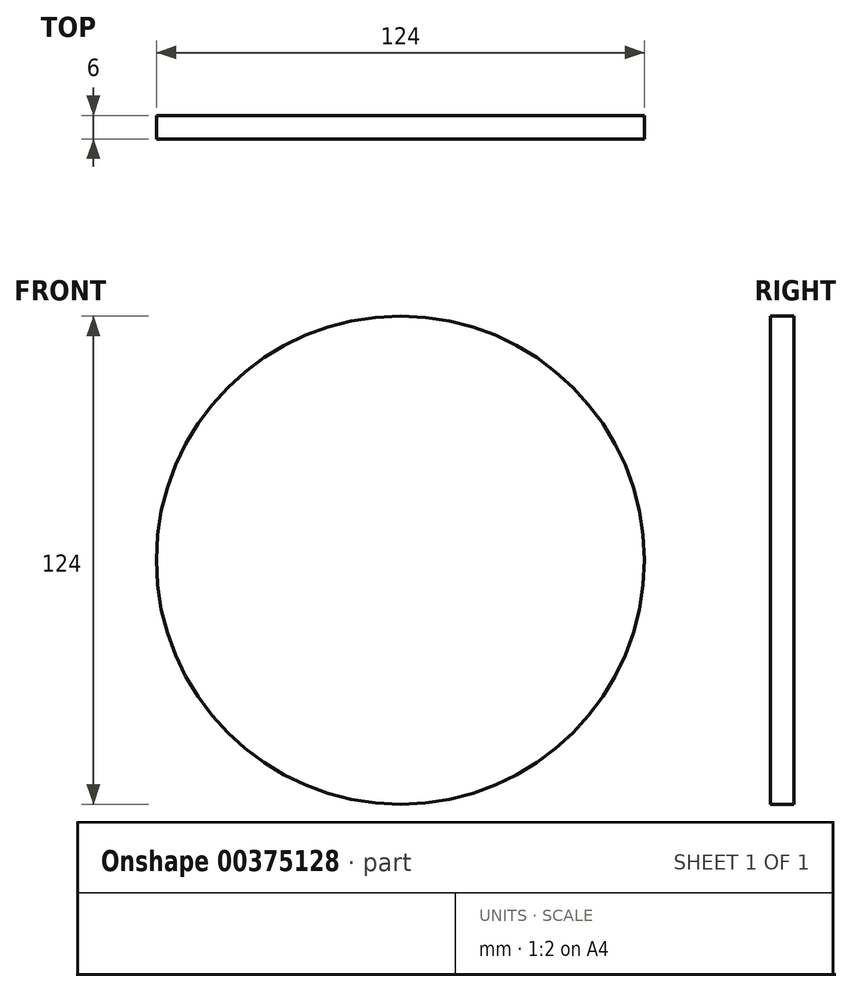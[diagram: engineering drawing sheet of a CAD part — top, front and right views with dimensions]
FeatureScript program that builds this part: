
annotation { "Feature Type Name" : "Feature", "Feature Type Description" : "" }
export const myFeature = defineFeature(function(context is Context, id is Id, definition is map)
    precondition{}
    {
        {
            var Q0;
            Q0=qCreatedBy(makeId("Front.planeOp"),FACE);
            var sketch = newSketch(context, id + "F0", { "sketchPlane" : qUnion([Q0])});
            skCircle(sketch, "E0", {"center": v(-17.64, 6.35) * mm, "radius": 62 * mm});
            skSolve(sketch);
        }
        {
            var Q0;
            Q0 = qSketchRegion(id + "F0", true);
            extrude(context, id + "F1", {"entities" : qUnion([Q0]), "oppositeDirection" : true, "depth" : 6 * mm});
        }
    });
